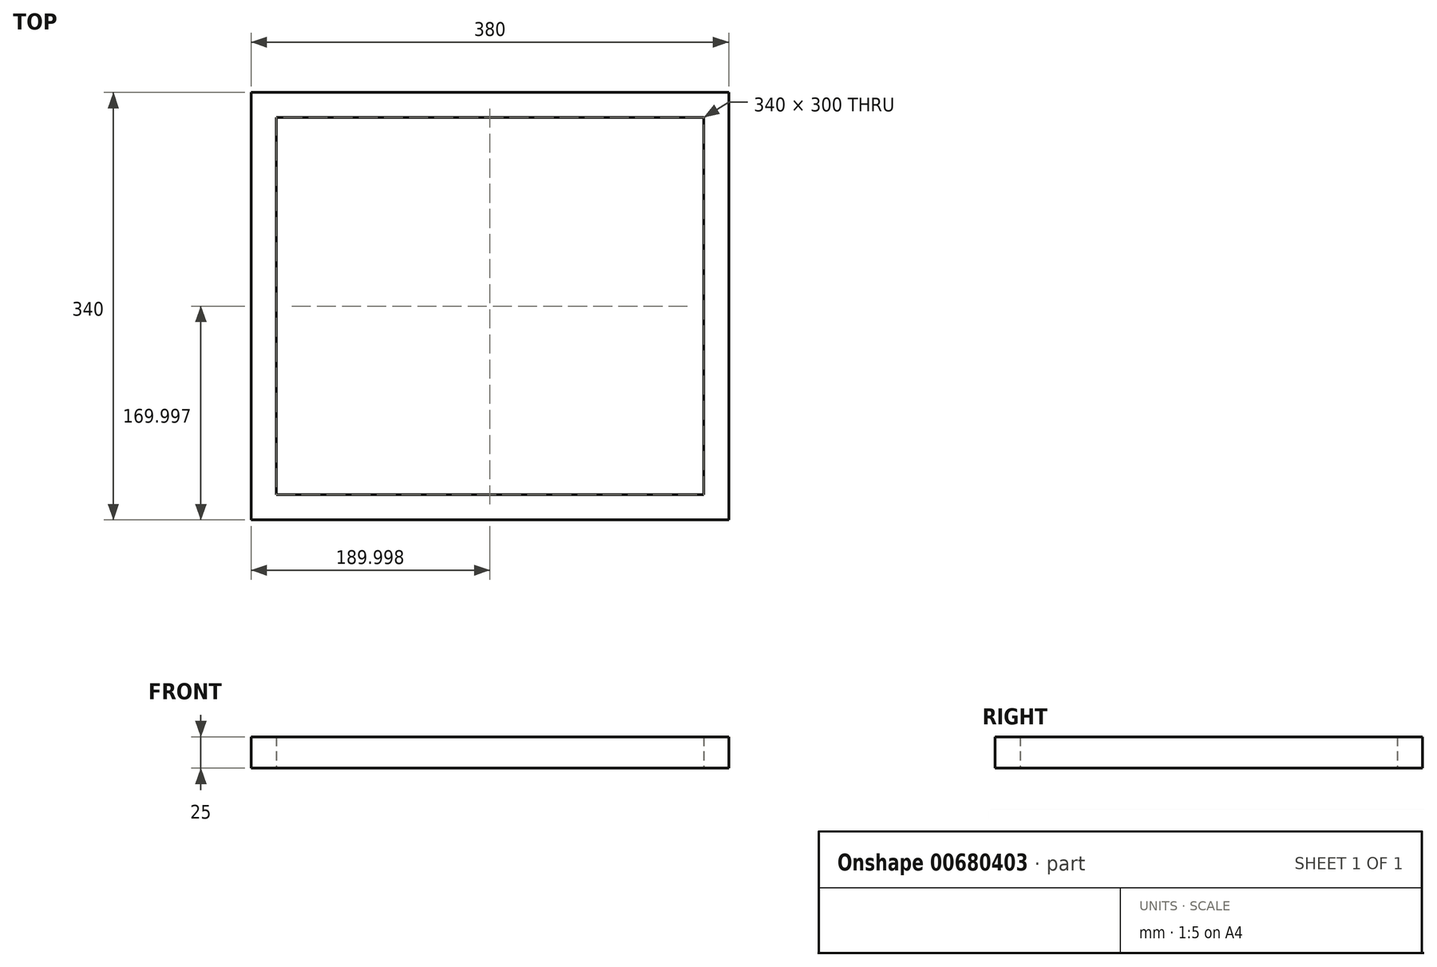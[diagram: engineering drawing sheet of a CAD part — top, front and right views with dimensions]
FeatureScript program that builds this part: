
annotation { "Feature Type Name" : "Feature", "Feature Type Description" : "" }
export const myFeature = defineFeature(function(context is Context, id is Id, definition is map)
    precondition{}
    {
        {
            var Q0;
            Q0=qCreatedBy(makeId("Top.planeOp"),FACE);
            var sketch = newSketch(context, id + "F0", { "sketchPlane" : qUnion([Q0])});
            skLineSegment(sketch, "E0.bottom", {"start": v(-323.6, 293.23) * mm, "end": v(56.4, 293.23) * mm});
            skLineSegment(sketch, "E0.top", {"start": v(-323.6, -46.77) * mm, "end": v(56.4, -46.77) * mm});
            skLineSegment(sketch, "E0.left", {"start": v(-323.6, 293.23) * mm, "end": v(-323.6, -46.77) * mm});
            skLineSegment(sketch, "E0.right", {"start": v(56.4, 293.23) * mm, "end": v(56.4, -46.77) * mm});
            skLineSegment(sketch, "E1.bottom", {"start": v(-303.6, 273.23) * mm, "end": v(36.4, 273.23) * mm});
            skLineSegment(sketch, "E1.top", {"start": v(-303.6, -26.77) * mm, "end": v(36.4, -26.77) * mm});
            skLineSegment(sketch, "E1.left", {"start": v(-303.6, 273.23) * mm, "end": v(-303.6, -26.77) * mm});
            skLineSegment(sketch, "E1.right", {"start": v(36.4, 273.23) * mm, "end": v(36.4, -26.77) * mm});
            skSolve(sketch);
        }
        {
            var Q0;
            Q0=makeQuery(id+"F0.imprint","IMPRINT",FACE,{"disambiguationData":[TD([[makeQuery(id+"F0.imprint","IMPRINT",EDGE,{"derivedFrom":sQuery(id+"F0.wireOp",EDGE,"E0.bottom")}),-1.0]])]});
            extrude(context, id + "F1", {"entities" : qUnion([Q0]), "depth" : 25 * mm, "offsetDistance" : 25 * mm});
        }
    });
